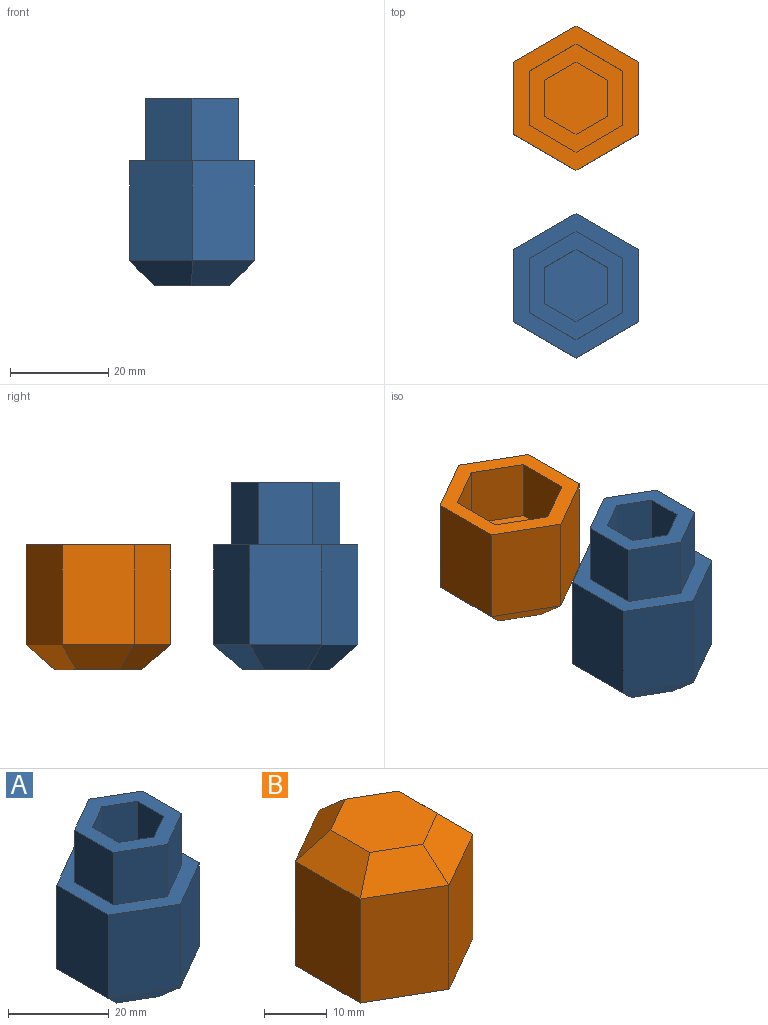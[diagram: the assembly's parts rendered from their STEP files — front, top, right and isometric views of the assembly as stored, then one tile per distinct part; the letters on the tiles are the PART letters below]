
ASSEMBLY  parts=2 mates=1
PART A: 28 faces, bbox 25.4x29.3x38.1 mm
  f0: plane 20.32x12.7mm, normal (0.5,-0.87,0), area 298mm2, adj f1,f5,f7,f27
  f1: plane 20.32x14.66mm, normal (1,0,0), area 298mm2, adj f0,f2,f7,f26
  f2: plane 20.32x12.7mm, normal (0.5,0.87,0), area 298mm2, adj f1,f3,f7,f24
  f3: plane 20.32x12.7mm, normal (-0.5,0.87,0), area 298mm2, adj f2,f4,f7,f22
  f4: plane 20.32x14.66mm, normal (-1,0,0), area 298mm2, adj f3,f5,f7,f23
  f5: plane 20.32x12.7mm, normal (-0.5,-0.87,0), area 298mm2, adj f0,f4,f7,f25
  f6: plane 17.6x15.24mm, normal (0,0,-1), area 201.1mm2, adj f22,f23,f24,f25,f26,f27
  f7: plane 29.33x25.4mm, normal (0,0,1), area 244.4mm2, adj f0,f1,f2,f3,f4,f5,f8,f9
  f8: plane 12.7x9.53mm, normal (0.5,-0.87,0), area 139.7mm2, adj f7,f9,f13,f14
  f9: plane 12.7x11mm, normal (1,0,0), area 139.7mm2, adj f7,f8,f10,f14
  f10: plane 12.7x9.53mm, normal (0.5,0.87,0), area 139.7mm2, adj f7,f9,f11,f14
  f11: plane 12.7x9.53mm, normal (-0.5,0.87,0), area 139.7mm2, adj f7,f10,f12,f14
  f12: plane 12.7x11mm, normal (-1,0,0), area 139.7mm2, adj f7,f11,f13,f14
  f13: plane 12.7x9.53mm, normal (-0.5,-0.87,0), area 139.7mm2, adj f7,f8,f12,f14
  f14: plane 22x19.05mm, normal (0,0,1), area 174.6mm2, adj f8,f9,f10,f11,f12,f13,f16,f17
  f15: plane 14.66x12.7mm, normal (0,0,1), area 139.7mm2, adj f16,f17,f18,f19,f20,f21
  f16: plane 28.58x7.33mm, normal (-1,0,0), area 209.5mm2, adj f14,f15,f17,f21
  f17: plane 28.58x6.35mm, normal (-0.5,-0.87,0), area 209.5mm2, adj f14,f15,f16,f18
  f18: plane 28.58x6.35mm, normal (0.5,-0.87,0), area 209.5mm2, adj f14,f15,f17,f19
  f19: plane 28.58x7.33mm, normal (1,0,0), area 209.5mm2, adj f14,f15,f18,f20
  f20: plane 28.58x6.35mm, normal (0.5,0.87,0), area 209.5mm2, adj f14,f15,f19,f21
  f21: plane 28.58x6.35mm, normal (-0.5,0.87,0), area 209.5mm2, adj f14,f15,f16,f20
  f22: plane 12.7x10.27mm, normal (-0.35,0.61,-0.71), area 84.3mm2, adj f3,f6,f23,f24
  f23: plane 14.66x5.08mm, normal (-0.71,0,-0.71), area 84.3mm2, adj f4,f6,f22,f25
  f24: plane 12.7x10.27mm, normal (0.35,0.61,-0.71), area 84.3mm2, adj f2,f6,f22,f26
  f25: plane 12.7x10.27mm, normal (-0.35,-0.61,-0.71), area 84.3mm2, adj f5,f6,f23,f27
  f26: plane 14.66x5.08mm, normal (0.71,0,-0.71), area 84.3mm2, adj f1,f6,f24,f27
  f27: plane 12.7x10.27mm, normal (0.35,-0.61,-0.71), area 84.3mm2, adj f0,f6,f25,f26
PART B: 28 faces, bbox 25.4x29.3x25.4 mm
  f0: plane 29.33x25.4mm, normal (0,0,-1), area 244.4mm2, adj f2,f3,f4,f5,f6,f7,f8,f9
  f1: plane 17.6x15.24mm, normal (0,0,1), area 201.1mm2, adj f22,f23,f24,f25,f26,f27
  f2: plane 20.32x12.7mm, normal (-0.5,-0.87,0), area 298mm2, adj f0,f3,f7,f25
  f3: plane 20.32x14.66mm, normal (-1,0,0), area 298mm2, adj f0,f2,f4,f23
  f4: plane 20.32x12.7mm, normal (-0.5,0.87,0), area 298mm2, adj f0,f3,f5,f22
  f5: plane 20.32x12.7mm, normal (0.5,0.87,0), area 298mm2, adj f0,f4,f6,f24
  f6: plane 20.32x14.66mm, normal (1,0,0), area 298mm2, adj f0,f5,f7,f26
  f7: plane 20.32x12.7mm, normal (0.5,-0.87,0), area 298mm2, adj f0,f2,f6,f27
  f8: plane 12.7x9.53mm, normal (-0.5,0.87,0), area 139.7mm2, adj f0,f9,f13,f14
  f9: plane 12.7x11mm, normal (-1,0,0), area 139.7mm2, adj f0,f8,f10,f14
  f10: plane 12.7x9.53mm, normal (-0.5,-0.87,0), area 139.7mm2, adj f0,f9,f11,f14
  f11: plane 12.7x9.53mm, normal (0.5,-0.87,0), area 139.7mm2, adj f0,f10,f12,f14
  f12: plane 12.7x11mm, normal (1,0,0), area 139.7mm2, adj f0,f11,f13,f14
  f13: plane 12.7x9.53mm, normal (0.5,0.87,0), area 139.7mm2, adj f0,f8,f12,f14
  f14: plane 22x19.05mm, normal (0,0,-1), area 174.6mm2, adj f8,f9,f10,f11,f12,f13,f16,f17
  f15: plane 14.66x12.7mm, normal (0,0,-1), area 139.7mm2, adj f16,f17,f18,f19,f20,f21
  f16: plane 6.35x3.67mm, normal (0.5,0.87,0), area 23.3mm2, adj f14,f15,f17,f21
  f17: plane 7.33x3.18mm, normal (1,0,0), area 23.3mm2, adj f14,f15,f16,f18
  f18: plane 6.35x3.67mm, normal (0.5,-0.87,0), area 23.3mm2, adj f14,f15,f17,f19
  f19: plane 6.35x3.67mm, normal (-0.5,-0.87,0), area 23.3mm2, adj f14,f15,f18,f20
  f20: plane 7.33x3.18mm, normal (-1,0,0), area 23.3mm2, adj f14,f15,f19,f21
  f21: plane 6.35x3.67mm, normal (-0.5,0.87,0), area 23.3mm2, adj f14,f15,f16,f20
  f22: plane 12.7x10.27mm, normal (-0.35,0.61,0.71), area 84.3mm2, adj f1,f4,f23,f24
  f23: plane 14.66x5.08mm, normal (-0.71,0,0.71), area 84.3mm2, adj f1,f3,f22,f25
  f24: plane 12.7x10.27mm, normal (0.35,0.61,0.71), area 84.3mm2, adj f1,f5,f22,f26
  f25: plane 12.7x10.27mm, normal (-0.35,-0.61,0.71), area 84.3mm2, adj f1,f2,f23,f27
  f26: plane 14.66x5.08mm, normal (0.71,0,0.71), area 84.3mm2, adj f1,f6,f24,f27
  f27: plane 12.7x10.27mm, normal (0.35,-0.61,0.71), area 84.3mm2, adj f1,f7,f25,f26
PLACE A at identity
PLACE B rot(axis=(0,1,0),180deg) t=(0,38.1,50.8)mm
MATE fastened B.f1 <-> A.f6  axis (0,0,-1) through (0,38.1,0)mm
